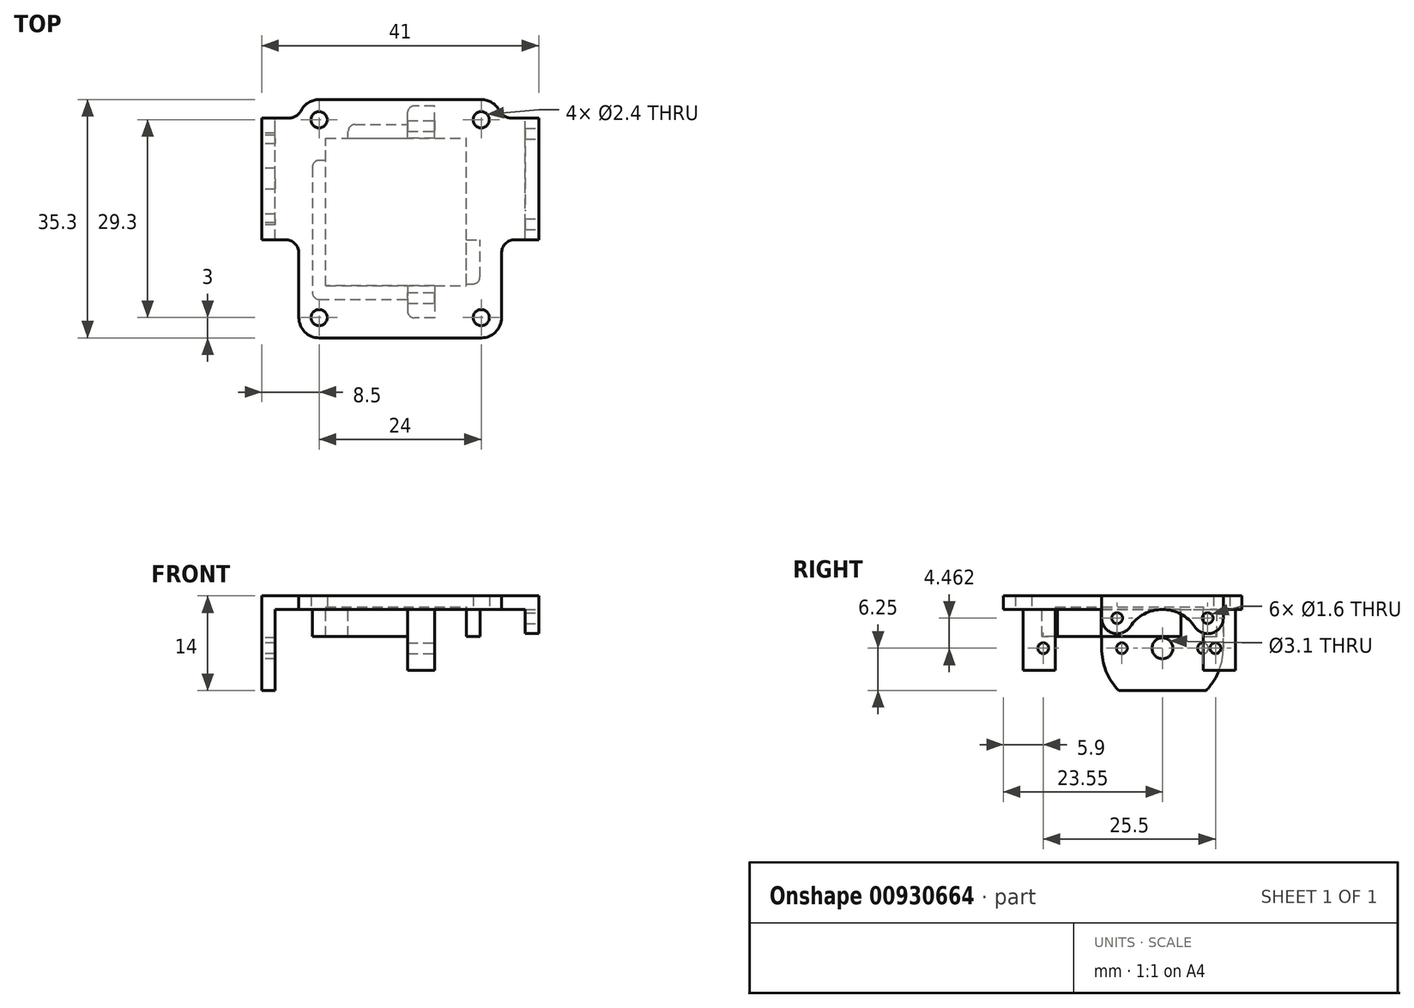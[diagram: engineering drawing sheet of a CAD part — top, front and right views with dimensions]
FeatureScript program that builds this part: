
annotation { "Feature Type Name" : "Feature", "Feature Type Description" : "" }
export const myFeature = defineFeature(function(context is Context, id is Id, definition is map)
    precondition{}
    {
        {
            var Q0;
            Q0=qCreatedBy(makeId("Top.planeOp"),FACE);
            var sketch = newSketch(context, id + "F0", { "sketchPlane" : qUnion([Q0])});
            skLineSegment(sketch, "E0.bottom", {"start": v(0, 0) * mm, "end": v(15.8, 0) * mm, "construction": true});
            skLineSegment(sketch, "E0.top", {"start": v(3, 21.3) * mm, "end": v(15.8, 21.3) * mm, "construction": true});
            skLineSegment(sketch, "E0.left", {"start": v(0, 0) * mm, "end": v(0, 18.3) * mm, "construction": true});
            skLineSegment(sketch, "E0.right", {"start": v(20.2, 0) * mm, "end": v(20.2, 21.3) * mm, "construction": true});
            skLineSegment(sketch, "E1.bottom", {"start": v(16.5, 25.35) * mm, "end": v(15.8, 25.35) * mm, "construction": true});
            skLineSegment(sketch, "E1.top", {"start": v(16.5, -4.05) * mm, "end": v(15.8, -4.05) * mm, "construction": true});
            skLineSegment(sketch, "E1.left", {"start": v(16.5, 25.35) * mm, "end": v(16.5, 21.3) * mm, "construction": true});
            skLineSegment(sketch, "E1.right", {"start": v(15.8, 25.35) * mm, "end": v(15.8, 21.3) * mm, "construction": true});
            skLineSegment(sketch, "E2.trimOffspring", {"start": v(16.5, 21.3) * mm, "end": v(20.2, 21.3) * mm, "construction": true});
            skLineSegment(sketch, "E3.trimOffspring", {"start": v(15.8, 0) * mm, "end": v(15.8, -4.05) * mm, "construction": true});
            skLineSegment(sketch, "E4.trimOffspring", {"start": v(16.5, 0) * mm, "end": v(16.5, -4.05) * mm, "construction": true});
            skLineSegment(sketch, "E5.trimOffspring", {"start": v(16.5, 0) * mm, "end": v(20.2, 0) * mm, "construction": true});
            skLineSegment(sketch, "E6", {"start": v(15.8, 23.4) * mm, "end": v(16.5, 23.4) * mm, "construction": true});
            skLineSegment(sketch, "E7", {"start": v(15.8, -2.1) * mm, "end": v(16.5, -2.1) * mm, "construction": true});
            skLineSegment(sketch, "E8", {"start": v(0, 18.3) * mm, "end": v(3, 21.3) * mm, "construction": true});
            skPoint(sketch, "E9.orphan", {"position": v(0, 21.3) * mm});
            skLineSegment(sketch, "E10", {"start": v(20.2, 21.3) * mm, "end": v(24.2, 21.3) * mm, "construction": true});
            skLineSegment(sketch, "E11", {"start": v(24.2, 21.3) * mm, "end": v(24.2, 6.8) * mm, "construction": true});
            skLineSegment(sketch, "E12", {"start": v(24.2, 6.8) * mm, "end": v(20.2, 6.8) * mm, "construction": true});
            skLineSegment(sketch, "E13", {"start": v(24.2, 15.55) * mm, "end": v(28.7, 15.55) * mm, "construction": true});
            skLineSegment(sketch, "E14.bottom", {"start": v(28.7, 21.3) * mm, "end": v(26.7, 21.3) * mm, "construction": true});
            skLineSegment(sketch, "E14.top", {"start": v(28.7, 0) * mm, "end": v(26.7, 0) * mm, "construction": true});
            skLineSegment(sketch, "E14.left", {"start": v(28.7, 21.3) * mm, "end": v(28.7, 0) * mm, "construction": true});
            skLineSegment(sketch, "E14.right", {"start": v(26.7, 21.3) * mm, "end": v(26.7, 0) * mm, "construction": true});
            skLineSegment(sketch, "E15.bottom", {"start": v(-7.3, 21.3) * mm, "end": v(-5.3, 21.3) * mm, "construction": true});
            skLineSegment(sketch, "E15.top", {"start": v(-7.3, 0) * mm, "end": v(-5.3, 0) * mm, "construction": true});
            skLineSegment(sketch, "E15.left", {"start": v(-7.3, 21.3) * mm, "end": v(-7.3, 0) * mm, "construction": true});
            skLineSegment(sketch, "E15.right", {"start": v(-5.3, 21.3) * mm, "end": v(-5.3, 0) * mm, "construction": true});
            skLineSegment(sketch, "E16", {"start": v(24.2, 18.55) * mm, "end": v(26.7, 18.55) * mm, "construction": true});
            skLineSegment(sketch, "E17", {"start": v(24.2, 12.55) * mm, "end": v(26.7, 12.55) * mm, "construction": true});
            skSolve(sketch);
        }
        {
            var Q0;
            Q0=qCreatedBy(makeId("Top.planeOp"),FACE);
            var sketch = newSketch(context, id + "F1", { "sketchPlane" : qUnion([Q0])});
            skLineSegment(sketch, "E18.left", {"start": v(-9.8, 24.55) * mm, "end": v(-9.8, 6.55) * mm});
            skLineSegment(sketch, "E18.right", {"start": v(31.2, 24.55) * mm, "end": v(31.2, 6.55) * mm});
            skLineSegment(sketch, "E19", {"start": v(10.7, 27.3) * mm, "end": v(10.7, -8) * mm, "construction": true});
            skCircle(sketch, "E20", {"center": v(-1.3, 24.3) * mm, "radius": 1.2 * mm});
            skCircle(sketch, "E21", {"center": v(22.7, 24.3) * mm, "radius": 1.2 * mm});
            skCircle(sketch, "E22", {"center": v(-1.3, -5) * mm, "radius": 1.2 * mm});
            skCircle(sketch, "E23", {"center": v(22.7, -5) * mm, "radius": 1.2 * mm});
            skLineSegment(sketch, "E24", {"start": v(-1.3, 24.3) * mm, "end": v(22.7, 24.3) * mm, "construction": true});
            skLineSegment(sketch, "E25", {"start": v(-1.3, 24.3) * mm, "end": v(-1.3, -5) * mm, "construction": true});
            skLineSegment(sketch, "E26", {"start": v(-1.3, -5) * mm, "end": v(22.7, -5) * mm, "construction": true});
            skLineSegment(sketch, "E27", {"start": v(22.7, -5) * mm, "end": v(22.7, 24.3) * mm, "construction": true});
            skArc(sketch, "E28", {"start": v(-1.3, 27.3) * mm, "mid": v(-3.33, 26.5) * mm, "end": v(-4.29, 24.55) * mm});
            skArc(sketch, "E29", {"start": v(25.69, 24.55) * mm, "mid": v(24.73, 26.5) * mm, "end": v(22.7, 27.3) * mm});
            skArc(sketch, "E30", {"start": v(-4.3, -5) * mm, "mid": v(-3.42, -7.12) * mm, "end": v(-1.3, -8) * mm});
            skArc(sketch, "E31", {"start": v(22.7, -8) * mm, "mid": v(24.82, -7.12) * mm, "end": v(25.7, -5) * mm});
            skLineSegment(sketch, "E32", {"start": v(-1.3, 27.3) * mm, "end": v(22.7, 27.3) * mm});
            skLineSegment(sketch, "E33", {"start": v(-4.3, -5) * mm, "end": v(-4.3, 6.55) * mm});
            skLineSegment(sketch, "E34", {"start": v(25.7, -5) * mm, "end": v(25.7, 6.55) * mm});
            skLineSegment(sketch, "E35", {"start": v(-1.3, -8) * mm, "end": v(22.7, -8) * mm});
            skLineSegment(sketch, "E36", {"start": v(-9.8, 24.55) * mm, "end": v(-4.29, 24.55) * mm});
            skLineSegment(sketch, "E37", {"start": v(25.69, 24.55) * mm, "end": v(31.2, 24.55) * mm});
            skLineSegment(sketch, "E38", {"start": v(-9.8, 6.55) * mm, "end": v(-4.3, 6.55) * mm});
            skLineSegment(sketch, "E39", {"start": v(25.7, 6.55) * mm, "end": v(31.2, 6.55) * mm});
            skSolve(sketch);
        }
        {
            var Q0;
            Q0=qSketchRegion(id+"F1",true);
            extrude(context, id + "F2", {"entities" : qUnion([Q0]), "depth" : 2 * mm, "offsetDistance" : 25 * mm});
        }
        {
            var Q0;
            Q0=makeQuery(id+"F2.opExtrude","SWEPT_EDGE",EDGE,{"disambiguationData":[OSD([sQuery(id+"F1.wireOp",EDGE,"E18.bottom"),sQuery(id+"F1.wireOp",EDGE,"n9spz6sa-SeqF-ro3C-UlOU-JdgqFO8XuwJj")])]});
            var Q1;
            Q1=makeQuery(id+"F2.opExtrude","SWEPT_EDGE",EDGE,{"disambiguationData":[OSD([sQuery(id+"F1.wireOp",EDGE,"v9wraEXt-J1L3-XLAm-fg3X-uzmLA6GDD1Q5"),sQuery(id+"F1.wireOp",EDGE,"3bf1b7fd-33ad-4c0a-b081-5d8ae0c3909f.trimOffspring")])]});
            var Q2;
            Q2=makeQuery(id+"F2.opExtrude","SWEPT_EDGE",EDGE,{"disambiguationData":[OSD([sQuery(id+"F1.wireOp",EDGE,"E34"),sQuery(id+"F1.wireOp",EDGE,"87065f72-439b-48f6-8dea-1321e7ddb749.trimOffspring")])]});
            var Q3;
            Q3=makeQuery(id+"F2.opExtrude","SWEPT_EDGE",EDGE,{"disambiguationData":[OSD([sQuery(id+"F1.wireOp",EDGE,"E18.top"),sQuery(id+"F1.wireOp",EDGE,"E33")])]});
            fillet(context, id + "F3", {"entities" : qUnion([Q0, Q1, Q2, Q3]), "radius" : 2 * mm, "tangentPropagation" : true, "allowEdgeOverflow" : false});
        }
        {
            var Q0;
            Q0=makeQuery(id+"F2.opExtrude","CAP_FACE",FACE,{"disambiguationData":[OSD([sQuery(id+"F1.wireOp",EDGE,"E18.bottom"),sQuery(id+"F1.wireOp",EDGE,"E18.top"),sQuery(id+"F1.wireOp",EDGE,"E18.left"),sQuery(id+"F1.wireOp",EDGE,"E18.right"),sQuery(id+"F1.wireOp",EDGE,"E20"),sQuery(id+"F1.wireOp",EDGE,"E21"),sQuery(id+"F1.wireOp",EDGE,"E22"),sQuery(id+"F1.wireOp",EDGE,"E23"),sQuery(id+"F1.wireOp",EDGE,"E28"),sQuery(id+"F1.wireOp",EDGE,"E29"),sQuery(id+"F1.wireOp",EDGE,"E30"),sQuery(id+"F1.wireOp",EDGE,"E31"),sQuery(id+"F1.wireOp",EDGE,"n9spz6sa-SeqF-ro3C-UlOU-JdgqFO8XuwJj"),sQuery(id+"F1.wireOp",EDGE,"E32"),sQuery(id+"F1.wireOp",EDGE,"v9wraEXt-J1L3-XLAm-fg3X-uzmLA6GDD1Q5"),sQuery(id+"F1.wireOp",EDGE,"E33"),sQuery(id+"F1.wireOp",EDGE,"E34"),sQuery(id+"F1.wireOp",EDGE,"E35"),sQuery(id+"F1.wireOp",EDGE,"3bf1b7fd-33ad-4c0a-b081-5d8ae0c3909f.trimOffspring"),sQuery(id+"F1.wireOp",EDGE,"87065f72-439b-48f6-8dea-1321e7ddb749.trimOffspring")])],"isStart":true});
            var sketch = newSketch(context, id + "F4", { "sketchPlane" : qUnion([Q0])});
            skLineSegment(sketch, "E40.bottom", {"start": v(15.8, 0.3) * mm, "end": v(11.8, 0.3) * mm});
            skLineSegment(sketch, "E40.top", {"start": v(15.8, 5.05) * mm, "end": v(11.8, 5.05) * mm});
            skLineSegment(sketch, "E40.left", {"start": v(15.8, 0.3) * mm, "end": v(15.8, 5.05) * mm});
            skLineSegment(sketch, "E40.right", {"start": v(11.8, 0.3) * mm, "end": v(11.8, 5.05) * mm});
            skLineSegment(sketch, "E41.bottom", {"start": v(15.8, -21.6) * mm, "end": v(11.8, -21.6) * mm});
            skLineSegment(sketch, "E41.top", {"start": v(15.8, -26.35) * mm, "end": v(11.8, -26.35) * mm});
            skLineSegment(sketch, "E41.left", {"start": v(15.8, -21.6) * mm, "end": v(15.8, -26.35) * mm});
            skLineSegment(sketch, "E41.right", {"start": v(11.8, -21.6) * mm, "end": v(11.8, -26.35) * mm});
            skSolve(sketch);
        }
        {
            var Q0;
            Q0=qSketchRegion(id+"F4",true);
            extrude(context, id + "F5", {"entities" : qUnion([Q0]), "operationType" : NewBodyOperationType.ADD, "depth" : 9 * mm, "offsetDistance" : 25 * mm});
        }
        {
            var Q0;
            Q0=makeQuery(id+"F2.opExtrude","CAP_FACE",FACE,{"disambiguationData":[OSD([sQuery(id+"F1.wireOp",EDGE,"E18.bottom"),sQuery(id+"F1.wireOp",EDGE,"E18.top"),sQuery(id+"F1.wireOp",EDGE,"E18.left"),sQuery(id+"F1.wireOp",EDGE,"E18.right"),sQuery(id+"F1.wireOp",EDGE,"E20"),sQuery(id+"F1.wireOp",EDGE,"E21"),sQuery(id+"F1.wireOp",EDGE,"E22"),sQuery(id+"F1.wireOp",EDGE,"E23"),sQuery(id+"F1.wireOp",EDGE,"E28"),sQuery(id+"F1.wireOp",EDGE,"E29"),sQuery(id+"F1.wireOp",EDGE,"E30"),sQuery(id+"F1.wireOp",EDGE,"E31"),sQuery(id+"F1.wireOp",EDGE,"n9spz6sa-SeqF-ro3C-UlOU-JdgqFO8XuwJj"),sQuery(id+"F1.wireOp",EDGE,"E32"),sQuery(id+"F1.wireOp",EDGE,"v9wraEXt-J1L3-XLAm-fg3X-uzmLA6GDD1Q5"),sQuery(id+"F1.wireOp",EDGE,"E33"),sQuery(id+"F1.wireOp",EDGE,"E34"),sQuery(id+"F1.wireOp",EDGE,"E35"),sQuery(id+"F1.wireOp",EDGE,"3bf1b7fd-33ad-4c0a-b081-5d8ae0c3909f.trimOffspring"),sQuery(id+"F1.wireOp",EDGE,"87065f72-439b-48f6-8dea-1321e7ddb749.trimOffspring")])],"isStart":true});
            var sketch = newSketch(context, id + "F6", { "sketchPlane" : qUnion([Q0])});
            skLineSegment(sketch, "E42", {"start": v(-0.3, -18.3) * mm, "end": v(-2.3, -18.3) * mm});
            skLineSegment(sketch, "E43", {"start": v(-2.3, -18.3) * mm, "end": v(-2.3, 2.3) * mm});
            skLineSegment(sketch, "E44", {"start": v(-2.3, 2.3) * mm, "end": v(11.8, 2.3) * mm});
            skLineSegment(sketch, "E45", {"start": v(11.8, 2.3) * mm, "end": v(11.8, 0.3) * mm});
            skLineSegment(sketch, "E46", {"start": v(11.8, 0.3) * mm, "end": v(-0.3, 0.3) * mm});
            skLineSegment(sketch, "E47", {"start": v(-0.3, 0.3) * mm, "end": v(-0.3, -18.3) * mm});
            skLineSegment(sketch, "E48.bottom", {"start": v(3, -21.6) * mm, "end": v(11.8, -21.6) * mm});
            skLineSegment(sketch, "E48.top", {"start": v(3, -23.6) * mm, "end": v(11.8, -23.6) * mm});
            skLineSegment(sketch, "E48.left", {"start": v(3, -21.6) * mm, "end": v(3, -23.6) * mm});
            skLineSegment(sketch, "E48.right", {"start": v(11.8, -21.6) * mm, "end": v(11.8, -23.6) * mm});
            skLineSegment(sketch, "E49.bottom", {"start": v(20.5, 0) * mm, "end": v(22.5, 0) * mm});
            skLineSegment(sketch, "E49.top", {"start": v(20.5, -6.5) * mm, "end": v(22.5, -6.5) * mm});
            skLineSegment(sketch, "E49.left", {"start": v(20.5, 0) * mm, "end": v(20.5, -6.5) * mm});
            skLineSegment(sketch, "E49.right", {"start": v(22.5, 0) * mm, "end": v(22.5, -6.5) * mm});
            skSolve(sketch);
        }
        {
            var Q0;
            Q0=qSketchRegion(id+"F6",true);
            extrude(context, id + "F7", {"entities" : qUnion([Q0]), "operationType" : NewBodyOperationType.ADD, "depth" : 4 * mm, "offsetDistance" : 25 * mm});
        }
        {
            var Q0;
            Q0=makeQuery(id+"F5.opExtrude","SWEPT_FACE",FACE,{"disambiguationData":[OSD([sQuery(id+"F4.wireOp",EDGE,"E41.left")])]});
            var sketch = newSketch(context, id + "F8", { "sketchPlane" : qUnion([Q0])});
            skCircle(sketch, "E50", {"center": v(23.4, -5.75) * mm, "radius": 0.8 * mm});
            skCircle(sketch, "E51", {"center": v(-2.1, -5.75) * mm, "radius": 0.8 * mm});
            skSolve(sketch);
        }
        {
            var Q0;
            Q0=qSketchRegion(id+"F8",true);
            extrude(context, id + "F9", {"entities" : qUnion([Q0]), "operationType" : NewBodyOperationType.REMOVE, "endBound" : BoundingType.UP_TO_NEXT, "oppositeDirection" : true, "depth" : 25 * mm, "offsetDistance" : 25 * mm});
        }
        {
            var Q0;
            Q0=makeQuery(id+"F7.opExtrude","CAP_EDGE",EDGE,{"disambiguationData":[OSD([sQuery(id+"F6.wireOp",EDGE,"E45")])],"isStart":false});
            var Q1;
            Q1=makeQuery(id+"F7.opExtrude","SWEPT_EDGE",EDGE,{"disambiguationData":[OSD([sQuery(id+"F4.wireOp",EDGE,"E40.right"),sQuery(id+"F6.wireOp",EDGE,"E44"),sQuery(id+"F6.wireOp",EDGE,"E45")])]});
            var Q2;
            Q2=makeQuery(id+"F7.opExtrude","SWEPT_EDGE",EDGE,{"disambiguationData":[OSD([sQuery(id+"F6.wireOp",EDGE,"E43"),sQuery(id+"F6.wireOp",EDGE,"E44")])]});
            var Q3;
            Q3=makeQuery(id+"F7.opExtrude","SWEPT_EDGE",EDGE,{"disambiguationData":[OSD([sQuery(id+"F6.wireOp",EDGE,"E42"),sQuery(id+"F6.wireOp",EDGE,"E43")])]});
            var Q4;
            Q4=makeQuery(id+"F7.opExtrude","SWEPT_EDGE",EDGE,{"disambiguationData":[OSD([sQuery(id+"F6.wireOp",EDGE,"E48.top"),sQuery(id+"F6.wireOp",EDGE,"E48.left")])]});
            var Q5;
            Q5=makeQuery(id+"F7.opExtrude","SWEPT_EDGE",EDGE,{"disambiguationData":[OSD([sQuery(id+"F4.wireOp",EDGE,"E41.right"),sQuery(id+"F6.wireOp",EDGE,"E48.top"),sQuery(id+"F6.wireOp",EDGE,"E48.right")])]});
            var Q6;
            Q6=makeQuery(id+"F7.opExtrude","CAP_EDGE",EDGE,{"disambiguationData":[OSD([sQuery(id+"F6.wireOp",EDGE,"E48.right")])],"isStart":false});
            var Q7;
            Q7=makeQuery(id+"F7.opExtrude","SWEPT_EDGE",EDGE,{"disambiguationData":[OSD([sQuery(id+"F6.wireOp",EDGE,"E49.bottom"),sQuery(id+"F6.wireOp",EDGE,"E49.right")])]});
            var Q8;
            Q8=makeQuery(id+"F5.opExtrude","SWEPT_EDGE",EDGE,{"disambiguationData":[OSD([sQuery(id+"F4.wireOp",EDGE,"E41.top"),sQuery(id+"F4.wireOp",EDGE,"E41.right")])]});
            var Q9;
            Q9=makeQuery(id+"F5.opExtrude","SWEPT_EDGE",EDGE,{"disambiguationData":[OSD([sQuery(id+"F4.wireOp",EDGE,"E40.top"),sQuery(id+"F4.wireOp",EDGE,"E40.right")])]});
            fillet(context, id + "F10", {"entities" : qUnion([Q0, Q1, Q2, Q3, Q4, Q5, Q6, Q7, Q8, Q9]), "radius" : 1 * mm, "tangentPropagation" : true, "allowEdgeOverflow" : false});
        }
        {
            var Q0;
            Q0=makeQuery(id+"F2.opExtrude","CAP_FACE",FACE,{"disambiguationData":[OSD([sQuery(id+"F1.wireOp",EDGE,"E18.bottom"),sQuery(id+"F1.wireOp",EDGE,"E18.top"),sQuery(id+"F1.wireOp",EDGE,"E18.left"),sQuery(id+"F1.wireOp",EDGE,"E18.right"),sQuery(id+"F1.wireOp",EDGE,"E20"),sQuery(id+"F1.wireOp",EDGE,"E21"),sQuery(id+"F1.wireOp",EDGE,"E22"),sQuery(id+"F1.wireOp",EDGE,"E23"),sQuery(id+"F1.wireOp",EDGE,"E28"),sQuery(id+"F1.wireOp",EDGE,"E29"),sQuery(id+"F1.wireOp",EDGE,"E30"),sQuery(id+"F1.wireOp",EDGE,"E31"),sQuery(id+"F1.wireOp",EDGE,"n9spz6sa-SeqF-ro3C-UlOU-JdgqFO8XuwJj"),sQuery(id+"F1.wireOp",EDGE,"E32"),sQuery(id+"F1.wireOp",EDGE,"v9wraEXt-J1L3-XLAm-fg3X-uzmLA6GDD1Q5"),sQuery(id+"F1.wireOp",EDGE,"E33"),sQuery(id+"F1.wireOp",EDGE,"E34"),sQuery(id+"F1.wireOp",EDGE,"E35"),sQuery(id+"F1.wireOp",EDGE,"3bf1b7fd-33ad-4c0a-b081-5d8ae0c3909f.trimOffspring"),sQuery(id+"F1.wireOp",EDGE,"87065f72-439b-48f6-8dea-1321e7ddb749.trimOffspring")])],"isStart":true});
            var sketch = newSketch(context, id + "F11", { "sketchPlane" : qUnion([Q0])});
            skLineSegment(sketch, "E52.bottom", {"start": v(-9.8, -6.55) * mm, "end": v(-7.8, -6.55) * mm});
            skLineSegment(sketch, "E52.top", {"start": v(-9.8, -24.55) * mm, "end": v(-7.8, -24.55) * mm});
            skLineSegment(sketch, "E52.left", {"start": v(-9.8, -6.55) * mm, "end": v(-9.8, -24.55) * mm});
            skLineSegment(sketch, "E52.right", {"start": v(-7.8, -6.55) * mm, "end": v(-7.8, -24.55) * mm});
            skLineSegment(sketch, "E53.bottom", {"start": v(31.2, -6.55) * mm, "end": v(29.2, -6.55) * mm});
            skLineSegment(sketch, "E53.top", {"start": v(31.2, -24.55) * mm, "end": v(29.2, -24.55) * mm});
            skLineSegment(sketch, "E53.left", {"start": v(31.2, -6.55) * mm, "end": v(31.2, -24.55) * mm});
            skLineSegment(sketch, "E53.right", {"start": v(29.2, -6.55) * mm, "end": v(29.2, -24.55) * mm});
            skSolve(sketch);
        }
        {
            var Q0;
            Q0=qSketchRegion(id+"F11",true);
            extrude(context, id + "F12", {"entities" : qUnion([Q0]), "operationType" : NewBodyOperationType.ADD, "depth" : 12 * mm, "offsetDistance" : 25 * mm});
        }
        {
            var Q0;
            Q0=makeQuery(id+"F12.boolean.opBoolean","MERGE",FACE,{"derivedFrom":[makeQuery(id+"F2.opExtrude","SWEPT_FACE",FACE,{"disambiguationData":[OSD([sQuery(id+"F1.wireOp",EDGE,"E18.left")])]}),makeQuery(id+"F12.opExtrude","SWEPT_FACE",FACE,{"disambiguationData":[OSD([sQuery(id+"F11.wireOp",EDGE,"E52.left")])]})]});
            var sketch = newSketch(context, id + "F13", { "sketchPlane" : qUnion([Q0])});
            skCircle(sketch, "E54", {"center": v(-15.55, -5.75) * mm, "radius": 1.55 * mm});
            skLineSegment(sketch, "E55", {"start": v(-24.55, -5.75) * mm, "end": v(-6.55, -5.75) * mm, "construction": true});
            skCircle(sketch, "E56", {"center": v(-21.55, -5.75) * mm, "radius": 0.8 * mm});
            skCircle(sketch, "E57", {"center": v(-9.55, -5.75) * mm, "radius": 0.8 * mm});
            skArc(sketch, "E58", {"start": v(-24.55, -5.75) * mm, "mid": v(-23.9, -9.12) * mm, "end": v(-22.03, -12) * mm});
            skArc(sketch, "E59", {"start": v(-9.07, -12) * mm, "mid": v(-7.2, -9.12) * mm, "end": v(-6.55, -5.75) * mm});
            skLineSegment(sketch, "E60", {"start": v(-24.55, -5.75) * mm, "end": v(-24.55, -12) * mm});
            skLineSegment(sketch, "E61", {"start": v(-24.55, -12) * mm, "end": v(-22.03, -12) * mm});
            skLineSegment(sketch, "E62", {"start": v(-9.07, -12) * mm, "end": v(-6.55, -12) * mm});
            skLineSegment(sketch, "E63", {"start": v(-6.55, -12) * mm, "end": v(-6.55, -5.75) * mm});
            skSolve(sketch);
        }
        {
            var Q0;
            Q0=qSketchRegion(id+"F13",true);
            extrude(context, id + "F14", {"entities" : qUnion([Q0]), "operationType" : NewBodyOperationType.REMOVE, "endBound" : BoundingType.UP_TO_NEXT, "oppositeDirection" : true, "depth" : 25 * mm, "offsetDistance" : 25 * mm});
        }
        {
            var Q0;
            Q0=makeQuery(id+"F12.boolean.opBoolean","MERGE",FACE,{"derivedFrom":[makeQuery(id+"F2.opExtrude","SWEPT_FACE",FACE,{"disambiguationData":[OSD([sQuery(id+"F1.wireOp",EDGE,"E18.right")])]}),makeQuery(id+"F12.opExtrude","SWEPT_FACE",FACE,{"disambiguationData":[OSD([sQuery(id+"F11.wireOp",EDGE,"E53.left")])]})]});
            var sketch = newSketch(context, id + "F15", { "sketchPlane" : qUnion([Q0])});
            skCircle(sketch, "E64", {"center": v(15.55, -5.75) * mm, "radius": 5.5 * mm, "construction": true});
            skLineSegment(sketch, "E65", {"start": v(6.55, -5.75) * mm, "end": v(24.55, -5.75) * mm, "construction": true});
            skArc(sketch, "E66", {"start": v(20.34, -2.56) * mm, "mid": v(15.55, 0) * mm, "end": v(10.76, -2.56) * mm});
            skArc(sketch, "E67", {"start": v(11.05, -2.59) * mm, "mid": v(8.73, -6.04) * mm, "end": v(6.55, -9.6) * mm, "construction": true});
            skCircle(sketch, "E68", {"center": v(8.85, -1.29) * mm, "radius": 0.8 * mm});
            skArc(sketch, "E69", {"start": v(20.37, -8.4) * mm, "mid": v(19.48, -10.17) * mm, "end": v(18.74, -12) * mm, "construction": true});
            skCircle(sketch, "E70", {"center": v(22.25, -1.29) * mm, "radius": 0.8 * mm});
            skLineSegment(sketch, "E71", {"start": v(6.55, -12) * mm, "end": v(24.55, -12) * mm});
            skArc(sketch, "E72", {"start": v(6.55, -1.29) * mm, "mid": v(8.18, -3.49) * mm, "end": v(10.76, -2.56) * mm});
            skLineSegment(sketch, "E73", {"start": v(6.55, -1.29) * mm, "end": v(6.55, -12) * mm});
            skArc(sketch, "E74", {"start": v(20.34, -2.56) * mm, "mid": v(22.92, -3.49) * mm, "end": v(24.55, -1.29) * mm});
            skLineSegment(sketch, "E75", {"start": v(24.55, -1.29) * mm, "end": v(24.55, -12) * mm});
            skSolve(sketch);
        }
        {
            var Q0;
            Q0=qSketchRegion(id+"F15",true);
            extrude(context, id + "F16", {"entities" : qUnion([Q0]), "operationType" : NewBodyOperationType.REMOVE, "endBound" : BoundingType.UP_TO_NEXT, "oppositeDirection" : true, "depth" : 25 * mm, "offsetDistance" : 25 * mm});
        }
        {
            var Q0;
            Q0=makeQuery(id+"F2.opExtrude","SWEPT_EDGE",EDGE,{"disambiguationData":[OSD([sQuery(id+"F1.wireOp",EDGE,"E28"),sQuery(id+"F1.wireOp",EDGE,"E36")])]});
            var Q1;
            Q1=makeQuery(id+"F2.opExtrude","SWEPT_EDGE",EDGE,{"disambiguationData":[OSD([sQuery(id+"F1.wireOp",EDGE,"E29"),sQuery(id+"F1.wireOp",EDGE,"E37")])]});
            fillet(context, id + "F17", {"entities" : qUnion([Q0, Q1]), "radius" : 2 * mm, "tangentPropagation" : true, "allowEdgeOverflow" : false});
        }
        {
            var Q0;
            Q0=makeQuery(id+"F2.opExtrude","CAP_FACE",FACE,{"disambiguationData":[OSD([sQuery(id+"F1.wireOp",EDGE,"E18.left"),sQuery(id+"F1.wireOp",EDGE,"E18.right"),sQuery(id+"F1.wireOp",EDGE,"E20"),sQuery(id+"F1.wireOp",EDGE,"E21"),sQuery(id+"F1.wireOp",EDGE,"E22"),sQuery(id+"F1.wireOp",EDGE,"E23"),sQuery(id+"F1.wireOp",EDGE,"E28"),sQuery(id+"F1.wireOp",EDGE,"E29"),sQuery(id+"F1.wireOp",EDGE,"E30"),sQuery(id+"F1.wireOp",EDGE,"E31"),sQuery(id+"F1.wireOp",EDGE,"E32"),sQuery(id+"F1.wireOp",EDGE,"E33"),sQuery(id+"F1.wireOp",EDGE,"E34"),sQuery(id+"F1.wireOp",EDGE,"E35"),sQuery(id+"F1.wireOp",EDGE,"E36"),sQuery(id+"F1.wireOp",EDGE,"E37"),sQuery(id+"F1.wireOp",EDGE,"E38"),sQuery(id+"F1.wireOp",EDGE,"E39")])],"isStart":true});
            var sketch = newSketch(context, id + "F18", { "sketchPlane" : qUnion([Q0])});
            skLineSegment(sketch, "E76.bottom", {"start": v(-0.3, 0.3) * mm, "end": v(20.5, 0.3) * mm});
            skLineSegment(sketch, "E76.top", {"start": v(-0.3, -21.6) * mm, "end": v(20.5, -21.6) * mm});
            skLineSegment(sketch, "E76.left", {"start": v(-0.3, 0.3) * mm, "end": v(-0.3, -21.6) * mm});
            skLineSegment(sketch, "E76.right", {"start": v(20.5, 0.3) * mm, "end": v(20.5, -21.6) * mm});
            skSolve(sketch);
        }
        {
            var Q0;
            Q0=qSketchRegion(id+"F18",true);
            extrude(context, id + "F19", {"entities" : qUnion([Q0]), "operationType" : NewBodyOperationType.REMOVE, "oppositeDirection" : true, "depth" : 0.4 * mm, "offsetDistance" : 25 * mm});
        }
    });
